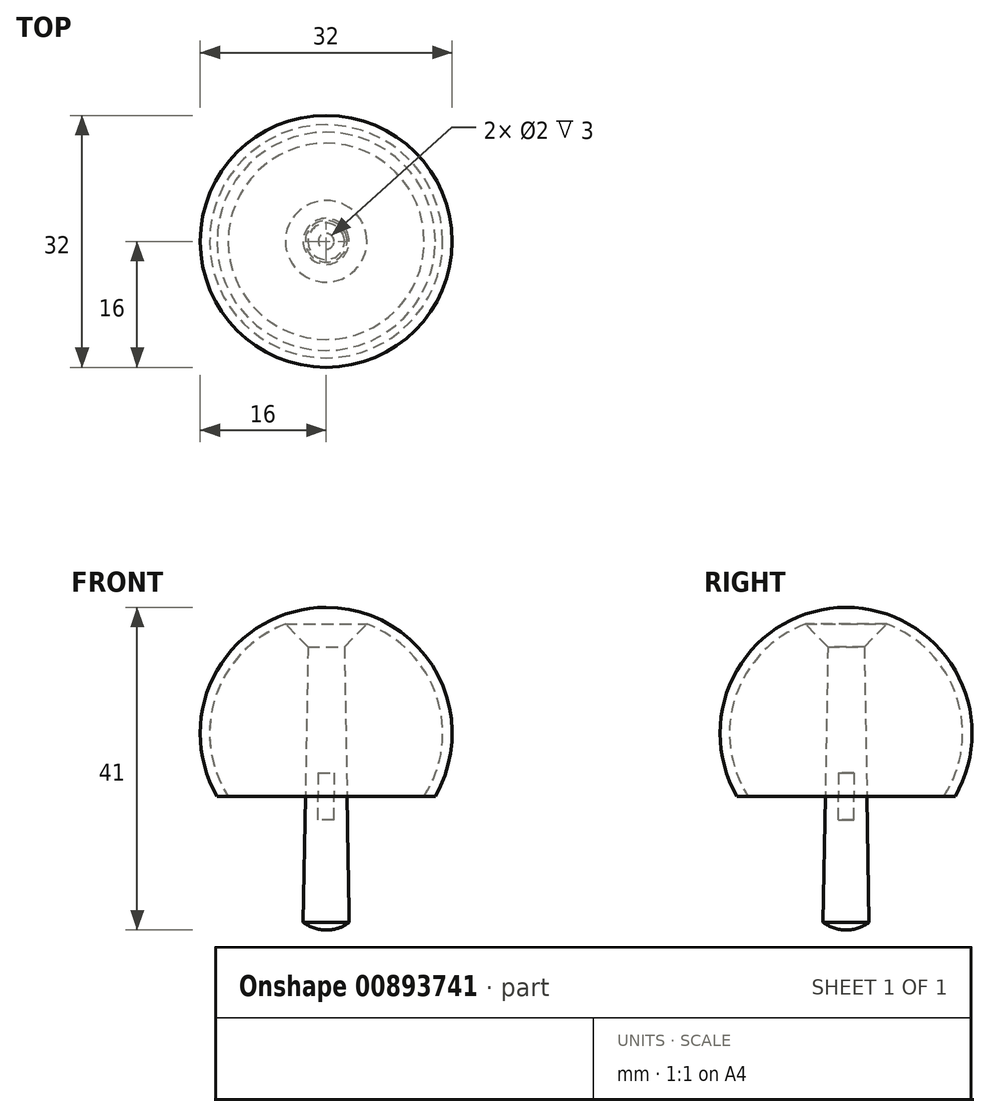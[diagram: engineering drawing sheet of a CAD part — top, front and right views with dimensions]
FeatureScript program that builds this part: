
annotation { "Feature Type Name" : "Feature", "Feature Type Description" : "" }
export const myFeature = defineFeature(function(context is Context, id is Id, definition is map)
    precondition{}
    {
        {
            var Q0;
            Q0=qCreatedBy(makeId("Front.planeOp"),FACE);
            var sketch = newSketch(context, id + "F0", { "sketchPlane" : qUnion([Q0])});
            skArc(sketch, "E0", {"start": v(0, 24) * mm, "mid": v(-13.86, 16) * mm, "end": v(-13.86, 0) * mm});
            skPoint(sketch, "E1", {"position": v(0, 24) * mm});
            skArc(sketch, "E2.0", {"start": v(0, 22.8) * mm, "mid": v(-12.99, 15.1) * mm, "end": v(-12.45, 0) * mm});
            skLineSegment(sketch, "E3", {"start": v(-13.86, 0) * mm, "end": v(-12.45, 0) * mm});
            skPoint(sketch, "E4.orphan", {"position": v(12.45, 0) * mm});
            skPoint(sketch, "E5.orphan", {"position": v(13.86, 0) * mm});
            skLineSegment(sketch, "E6", {"start": v(0, 22.8) * mm, "end": v(0, 24) * mm});
            skLineSegment(sketch, "E7", {"start": v(-2.25, 22.63) * mm, "end": v(-2.64, 0) * mm});
            skLineSegment(sketch, "E8", {"start": v(-2.64, 0) * mm, "end": v(0, 0) * mm});
            skLineSegment(sketch, "E9", {"start": v(0, 0) * mm, "end": v(0, 22.8) * mm});
            skLineSegment(sketch, "E10", {"start": v(-5.18, 21.86) * mm, "end": v(-2.31, 19) * mm});
            skSolve(sketch);
        }
        {
            var Q0;
            Q0=qSketchRegion(id+"F0",true);
            var Q1;
            Q1=sQuery(id+"F0.wireOp",EDGE,"E6");
            revolve(context, id + "F1", {"surfaceOperationType" : NewSurfaceOperationType.NEW, "entities" : qUnion([Q0]), "axis" : qUnion([Q1]), "revolveType" : RevolveType.FULL});
        }
        {
            var Q0;
            Q0=makeQuery(id+"F1.opRevolve","SWEPT_FACE",FACE,{"disambiguationData":[OSD([sQuery(id+"F0.wireOp",EDGE,"E8")])]});
            extrude(context, id + "F2", {"entities" : qUnion([Q0]), "depth" : 16 * mm, "offsetDistance" : 25 * mm, "hasDraft" : true, "draftAngle" : 1 * degree});
        }
        {
            var Q0;
            Q0=qCreatedBy(makeId("Front.planeOp"),FACE);
            var sketch = newSketch(context, id + "F3", { "sketchPlane" : qUnion([Q0])});
            skLineSegment(sketch, "E11", {"start": v(2.92, -16) * mm, "end": v(0, -16) * mm});
            skLineSegment(sketch, "E12", {"start": v(0, -16) * mm, "end": v(0, -17) * mm});
            skLineSegment(sketch, "E13", {"start": v(2.92, -17) * mm, "end": v(0, -17) * mm, "construction": true});
            skArc(sketch, "E14", {"start": v(0, -17) * mm, "mid": v(1.55, -16.74) * mm, "end": v(2.92, -16) * mm});
            skSolve(sketch);
        }
        {
            var Q0;
            Q0=makeQuery(id+"F3.imprint","IMPRINT",FACE,{"disambiguationData":[TD([[makeQuery(id+"F3.imprint","IMPRINT",EDGE,{"derivedFrom":sQuery(id+"F3.wireOp",EDGE,"E11")}),1.0]])]});
            var Q1;
            Q1=sQuery(id+"F3.wireOp",EDGE,"E12");
            revolve(context, id + "F4", {"operationType" : NewBodyOperationType.ADD, "surfaceOperationType" : NewSurfaceOperationType.NEW, "entities" : qUnion([Q0]), "axis" : qUnion([Q1]), "revolveType" : RevolveType.FULL});
        }
        {
            var Q0;
            Q0=makeQuery(id+"F2.opExtrude","CAP_FACE",FACE,{"disambiguationData":[OSD([sQuery(id+"F0.wireOp",EDGE,"E8")])],"isStart":true});
            var sketch = newSketch(context, id + "F5", { "sketchPlane" : qUnion([Q0])});
            skCircle(sketch, "E15", {"center": v(0, 0) * mm, "radius": 1 * mm});
            skSolve(sketch);
        }
        {
            var Q0;
            Q0=makeQuery(id+"F5.imprint","IMPRINT",FACE,{"disambiguationData":[TD([[makeQuery(id+"F5.imprint","IMPRINT",EDGE,{"derivedFrom":sQuery(id+"F5.wireOp",EDGE,"E15")}),1.0]])]});
            extrude(context, id + "F6", {"entities" : qUnion([Q0]), "operationType" : NewBodyOperationType.REMOVE, "oppositeDirection" : true, "depth" : 3 * mm, "offsetDistance" : 25 * mm});
        }
        {
            var Q0;
            Q0=makeQuery(id+"F1.opRevolve","SWEPT_FACE",FACE,{"disambiguationData":[OSD([sQuery(id+"F0.wireOp",EDGE,"E8")])]});
            var sketch = newSketch(context, id + "F7", { "sketchPlane" : qUnion([Q0])});
            skCircle(sketch, "E16", {"center": v(0, 0) * mm, "radius": 1 * mm});
            skSolve(sketch);
        }
        {
            var Q0;
            Q0=makeQuery(id+"F7.imprint","IMPRINT",FACE,{"disambiguationData":[TD([[makeQuery(id+"F7.imprint","IMPRINT",EDGE,{"derivedFrom":sQuery(id+"F7.wireOp",EDGE,"E16")}),1.0]])]});
            extrude(context, id + "F8", {"entities" : qUnion([Q0]), "operationType" : NewBodyOperationType.REMOVE, "oppositeDirection" : true, "depth" : 3 * mm, "offsetDistance" : 25 * mm});
        }
    });
